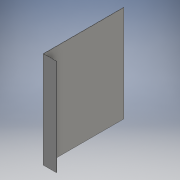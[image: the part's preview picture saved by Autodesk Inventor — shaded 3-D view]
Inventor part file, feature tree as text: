
AUTODESK INVENTOR PART (.ipt)
format: ipt  version: 2016 SP1 (Build 200210100, 210)  size: 88,576 bytes
history: native  units: mm
features: extrude x1, sketch x1
ambient origin geometry x8: Origin, YZ Plane, XZ Plane, XY Plane, X Axis, Y Axis, Z Axis, Center Point
bodies: Solid1 (feature_tree)
feature tree (2):
  extrude  "Extrusion1"  Depth=1.0mm
  sketch  "Sketch1"  dims[d0=250.0mm d1=1.0mm d2=249.0mm d3=40.0mm d4=300.0mm d5=0.0mm]
